# Revit family: Canopy_AustinMohawk_Tandem_2Row
name_source: partatom
category: Generic Models
units: mm (PartAtom-declared; Revit-internal decimal feet)

## family parameters
Always vertical = Yes
Can host rebar = No
Classification Number = 23.30.60.11.11.17
Cut with Voids When Loaded = No
Maintain Annotation Orientation = No
Part Type = Normal
Room Calculation Point = No
Round Connector Dimension = Use Diameter
Shared = No
Work Plane-Based = No

## types (1)
- ByType
    Assembly Code = F1010200
    Construction Details = http://www.arcat.com
    Deck Pan Width = 1' - 4"
    Default Elevation = 0' - 0"
    Description = Austin Mohawk Canopy - Type as specified in the Contract Documents
    Fascia Thickness = 0' - 1"
    Footing Material = Concrete - 4000psi
    Green Building-LEED = http://www.arcat.com
    Keynote = 10 73 16
    Manufacturer = Austin Mohawk
    Manufacturer Fax = 315-793-9370
    Manufacturer Website = http://www.austinmohawk.com
    Model = Canopy
    Product Data = http://www.arcat.com
    Product Properties = http://www.arcat.com
    Purlin Lateral Offset = 3' - 0"
    Purloffset = -0' - 4 15/16"
    Sales Information = http://www.austinmohawk.com
    Send Message = http://admin.arcat.com
    Specification = http://www.arcat.com
    StructCLOffset = 0' - 6 27/32"
    Structural Framing Material = Metal - Steel - ASTM A500 - Grade B - Rectangular and Square
    URL = http://www.austinmohawk.com
    ceilext = 1' - 0 7/8"
    faschang = 0' - 4"
    fascia = No
    ftgdpth = 4' - 0"
    ftgsz = 3' - 0"

## geometry (parser evidence)
native form markers: Blend x146, Sweep x51
no freeform markers — native parametric forms only
